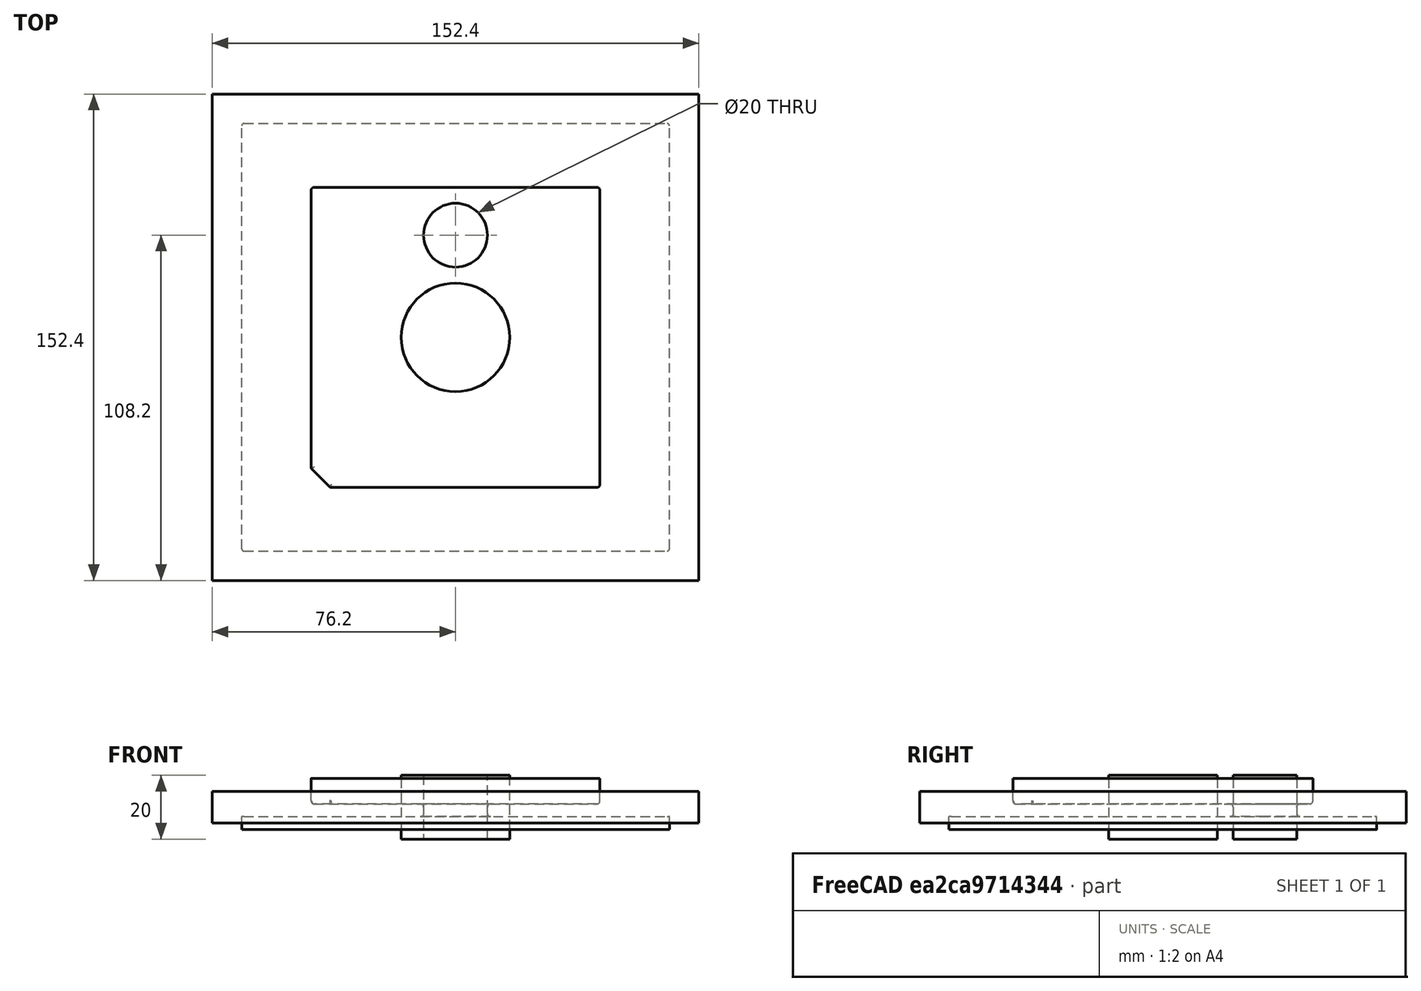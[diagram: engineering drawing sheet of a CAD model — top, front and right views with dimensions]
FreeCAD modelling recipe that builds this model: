
FCSTD DOCUMENT  (FreeCAD 1.0R39109 (Git))
Label: floppy_scan_frame_(no_sleeve)
License: All rights reserved
LicenseURL: http://en.wikipedia.org/wiki/All_rights_reserved
objects: PartDesign::Fillet×8, App::Part×5, PartDesign::Body×5, PartDesign::AdditiveBox×3, PartDesign::Chamfer×2, PartDesign::Boolean×2, PartDesign::AdditiveCylinder×2
note: 54 computed .brp shape members not serialized (recipe doc carries the construction recipe); baked Part::Feature solids carry a one-line shape summary decoded from their .brp

FEATURE [App::Part] Part001  label="3.5 floppy cutout"
  Origin = -> Origin003
FEATURE [PartDesign::AdditiveBox] Box
  AttacherType = Attacher::AttachEngine3D
  AttachmentOffset = pos=(-76.2,-76.2,0) rot=(0,0,1;0rad)
  AttachmentSupport = -> [XY_Plane002]
  Height = 10
  Length = 152.4
  MapMode = 5
  Placement = pos=(-76.2,-76.2,0) rot=(0,0,1;0rad)
  Suppressed = false
  Width = 152.4
FEATURE [PartDesign::AdditiveBox] Box001
  AttacherType = Attacher::AttachEngine3D
  AttachmentOffset = pos=(-45.25,-47,6) rot=(0,0,1;0rad)
  AttachmentSupport = -> [XY_Plane004]
  Height = 8
  Length = 90.5
  MapMode = 5
  Placement = pos=(-45.25,-47,6) rot=(0,0,1;0rad)
  Suppressed = false
  Width = 94
FEATURE [PartDesign::Chamfer] Chamfer
  Angle = 45
  Base = -> Box001 [Edge1]
  BaseFeature = -> Box001
  ChamferType = 0
  FlipDirection = false
  Placement = pos=(-45.25,-47,6) rot=(0,0,1;0rad)
  Size = 6
  Size2 = 1
  SupportTransform = false
  Suppressed = false
  UseAllEdges = false
FEATURE [PartDesign::Fillet] Fillet
  Base = -> Chamfer [Edge12,Edge3,Edge15]
  BaseFeature = -> Chamfer
  Placement = pos=(-45.25,-47,6) rot=(0,0,1;0rad)
  Radius = 1
  SupportTransform = false
  Suppressed = false
  UseAllEdges = false
FEATURE [PartDesign::Fillet] Fillet001
  Base = -> Fillet [Edge3,Edge15]
  BaseFeature = -> Fillet
  Placement = pos=(-45.25,-47,6) rot=(0,0,1;0rad)
  Radius = 0.5
  SupportTransform = false
  Suppressed = false
  UseAllEdges = false
FEATURE [PartDesign::Fillet] Fillet002
  Base = -> Fillet001 [Edge4,Edge14,Edge18,Edge22,Edge20,Edge24,Edge23,Edge21,Edge19,Edge16]
  BaseFeature = -> Fillet001
  Placement = pos=(-45.25,-47,6) rot=(0,0,1;0rad)
  Radius = 1
  SupportTransform = false
  Suppressed = false
  UseAllEdges = false
FEATURE [PartDesign::Body] Body
  AllowCompound = false
  Group = -> [Box001,Chamfer,Fillet,Fillet001,Fillet002]
  Origin = -> Origin004
  Tip = -> Fillet002
FEATURE [App::Part] Part002  label="5.25 floppy cutout"
  Origin = -> Origin005
FEATURE [PartDesign::AdditiveBox] Box002
  AttacherType = Attacher::AttachEngine3D
  AttachmentOffset = pos=(-67,-67,-2) rot=(0,0,1;0rad)
  AttachmentSupport = -> [XY_Plane006]
  Height = 4
  Length = 134
  MapMode = 5
  Placement = pos=(-67,-67,-2) rot=(0,0,1;0rad)
  Suppressed = false
  Width = 134
FEATURE [PartDesign::Chamfer] Chamfer001
  Angle = 45
  Base = -> Box002 [Edge1,Edge3,Edge7,Edge5]
  BaseFeature = -> Box002
  ChamferType = 0
  FlipDirection = false
  Placement = pos=(-67,-67,-2) rot=(0,0,1;0rad)
  Size = 0.5
  Size2 = 1
  SupportTransform = false
  Suppressed = false
  UseAllEdges = false
FEATURE [PartDesign::Fillet] Fillet003
  Base = -> Chamfer001 [Edge13,Edge2]
  BaseFeature = -> Chamfer001
  Placement = pos=(-67,-67,-2) rot=(0,0,1;0rad)
  Radius = 0.5
  SupportTransform = false
  Suppressed = false
  UseAllEdges = false
FEATURE [PartDesign::Fillet] Fillet004
  Base = -> Fillet003 [Edge30,Edge29]
  BaseFeature = -> Fillet003
  Placement = pos=(-67,-67,-2) rot=(0,0,1;0rad)
  Radius = 0.5
  SupportTransform = false
  Suppressed = false
  UseAllEdges = false
FEATURE [PartDesign::Fillet] Fillet005
  Base = -> Fillet004 [Edge28,Edge33]
  BaseFeature = -> Fillet004
  Placement = pos=(-67,-67,-2) rot=(0,0,1;0rad)
  Radius = 0.5
  SupportTransform = false
  Suppressed = false
  UseAllEdges = false
FEATURE [PartDesign::Fillet] Fillet006
  Base = -> Fillet005 [Edge35,Edge31]
  BaseFeature = -> Fillet005
  Placement = pos=(-67,-67,-2) rot=(0,0,1;0rad)
  Radius = 0.5
  SupportTransform = false
  Suppressed = false
  UseAllEdges = false
FEATURE [PartDesign::Body] Body002
  AllowCompound = false
  Group = -> [Box002,Chamfer001,Fillet003,Fillet004,Fillet005,Fillet006]
  Origin = -> Origin006
  Tip = -> Fillet006
FEATURE [App::Part] Part003  label="5.25 sleeve cutout"
  Origin = -> Origin007
FEATURE [PartDesign::Boolean] Boolean
  BaseFeature = -> Box
  Group = -> [Body]
  Suppressed = false
  Type = 1
  UsePlacement = false
FEATURE [PartDesign::AdditiveCylinder] Cylinder001
  Angle = 360
  AttacherType = Attacher::AttachEngine3D
  AttachmentOffset = pos=(0,0,-5) rot=(0,0,1;0rad)
  AttachmentSupport = -> [XY_Plane011]
  FirstAngle = 0
  Height = 20
  MapMode = 5
  Placement = pos=(0,0,-5) rot=(0,0,1;0rad)
  Radius = 17
  SecondAngle = 0
  Suppressed = false
FEATURE [PartDesign::Body] Body005
  AllowCompound = false
  Group = -> [Cylinder001]
  Origin = -> Origin011
  Tip = -> Cylinder001
FEATURE [App::Part] Part004  label="finger hole"
  Group = -> [Body005]
  Origin = -> Origin009
FEATURE [PartDesign::AdditiveCylinder] Cylinder
  Angle = 360
  AttacherType = Attacher::AttachEngine3D
  AttachmentOffset = pos=(0,32,-5) rot=(0,0,1;0rad)
  AttachmentSupport = -> [XY_Plane010]
  FirstAngle = 0
  Height = 20
  MapMode = 5
  Placement = pos=(0,32,-5) rot=(0,0,1;0rad)
  Radius = 10
  SecondAngle = 0
  Suppressed = false
FEATURE [PartDesign::Body] Body004
  AllowCompound = false
  Group = -> [Cylinder]
  Origin = -> Origin010
  Tip = -> Cylinder
FEATURE [PartDesign::Boolean] Boolean001
  BaseFeature = -> Boolean
  Group = -> [Body002,Body004]
  Suppressed = false
  Type = 1
  UsePlacement = false
FEATURE [PartDesign::Fillet] Fillet007
  Base = -> Boolean001 [Face45]
  BaseFeature = -> Boolean001
  Radius = 1
  SupportTransform = false
  Suppressed = false
  UseAllEdges = false
FEATURE [PartDesign::Body] Body001  label="base"
  AllowCompound = false
  Group = -> [Box,Boolean,Boolean001,Fillet007]
  Origin = -> Origin002
  Tip = -> Fillet007
FEATURE [App::Part] Part  label="base001"
  Group = -> [Body001]
  Origin = -> Origin
